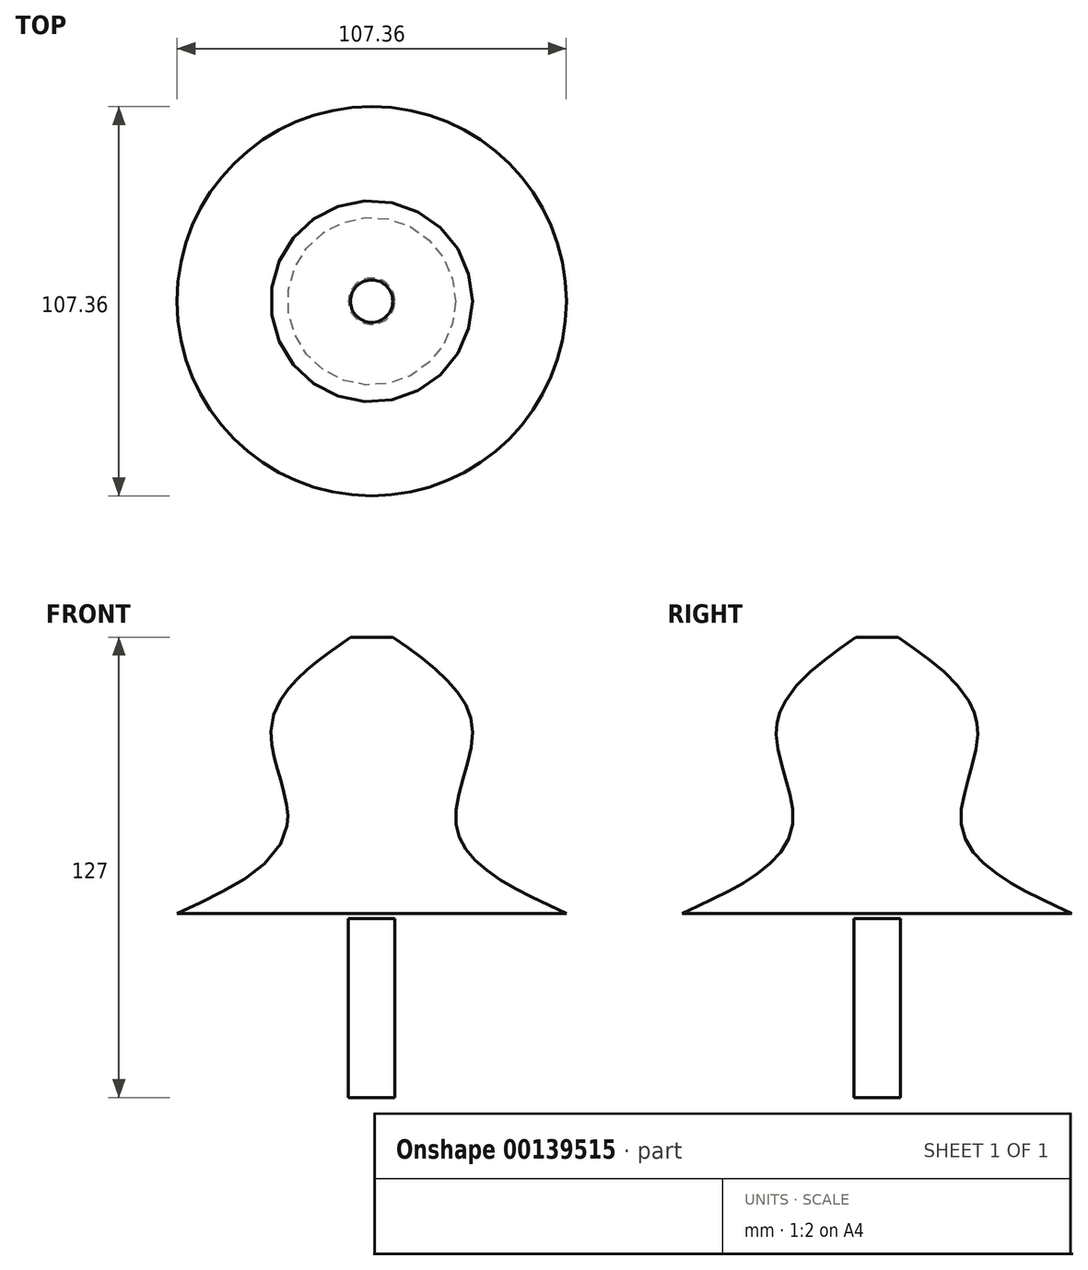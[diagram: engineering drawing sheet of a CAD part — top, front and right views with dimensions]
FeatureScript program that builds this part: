
annotation { "Feature Type Name" : "Feature", "Feature Type Description" : "" }
export const myFeature = defineFeature(function(context is Context, id is Id, definition is map)
    precondition{}
    {
        {
            var Q0;
            Q0=qCreatedBy(makeId("Top.planeOp"),FACE);
            cPlane(context, id + "F0", {"entities" : qUnion([Q0]), "cplaneType" : CPlaneType.OFFSET, "offset" : 25.4 * mm, "width" : 152.4 * mm, "height" : 152.4 * mm});
        }
        {
            var Q0;
            Q0=qCreatedBy(id+"F0.planeOp",FACE);
            cPlane(context, id + "F1", {"entities" : qUnion([Q0]), "cplaneType" : CPlaneType.OFFSET, "offset" : 25.4 * mm, "width" : 152.4 * mm, "height" : 152.4 * mm});
        }
        {
            var Q0;
            Q0=qCreatedBy(makeId("Top.planeOp"),FACE);
            cPlane(context, id + "F2", {"entities" : qUnion([Q0]), "cplaneType" : CPlaneType.OFFSET, "offset" : 25.4 * mm, "oppositeDirection" : true, "width" : 152.4 * mm, "height" : 152.4 * mm});
        }
        {
            var Q0;
            Q0=qCreatedBy(makeId("Top.planeOp"),FACE);
            var sketch = newSketch(context, id + "F3", { "sketchPlane" : qUnion([Q0])});
            skCircle(sketch, "E0", {"center": v(0, 0) * mm, "radius": 23.17 * mm});
            skSolve(sketch);
        }
        {
            var Q0;
            Q0=qCreatedBy(id+"F0.planeOp",FACE);
            var sketch = newSketch(context, id + "F4", { "sketchPlane" : qUnion([Q0])});
            skCircle(sketch, "E1", {"center": v(0, 0) * mm, "radius": 27.75 * mm});
            skSolve(sketch);
        }
        {
            var Q0;
            Q0=qCreatedBy(id+"F1.planeOp",FACE);
            var sketch = newSketch(context, id + "F5", { "sketchPlane" : qUnion([Q0])});
            skCircle(sketch, "E2", {"center": v(0, 0) * mm, "radius": 5.83 * mm});
            skSolve(sketch);
        }
        {
            var Q0;
            Q0=qCreatedBy(id+"F2.planeOp",FACE);
            var sketch = newSketch(context, id + "F6", { "sketchPlane" : qUnion([Q0])});
            skCircle(sketch, "E3", {"center": v(0, 0) * mm, "radius": 53.68 * mm});
            skSolve(sketch);
        }
        {
            var Q0;
            Q0 = qSketchRegion(id + "F5", true);
            var Q1;
            Q1 = qSketchRegion(id + "F4", true);
            var Q2;
            Q2 = qSketchRegion(id + "F3", true);
            var Q3;
            Q3 = qSketchRegion(id + "F6", true);
            loft(context, id + "F7", {"sheetProfilesArray" : [{ "sheetProfileEntities" : qUnion([Q0]) }, { "sheetProfileEntities" : qUnion([Q1]) }, { "sheetProfileEntities" : qUnion([Q2]) }, { "sheetProfileEntities" : qUnion([Q3]) }]});
        }
        {
            var Q0;
            Q0=qCreatedBy(id+"F2.planeOp",FACE);
            cPlane(context, id + "F8", {"entities" : qUnion([Q0]), "cplaneType" : CPlaneType.OFFSET, "offset" : 50.8 * mm, "oppositeDirection" : true, "width" : 152.4 * mm, "height" : 152.4 * mm});
        }
        {
            var Q0;
            Q0=qCreatedBy(id+"F8.planeOp",FACE);
            var sketch = newSketch(context, id + "F9", { "sketchPlane" : qUnion([Q0])});
            skCircle(sketch, "E4", {"center": v(0, 0) * mm, "radius": 6.4 * mm});
            skSolve(sketch);
        }
        {
            var Q0;
            Q0 = qSketchRegion(id + "F9", true);
            extrude(context, id + "F10", {"entities" : qUnion([Q0]), "operationType" : NewBodyOperationType.ADD, "depth" : 49.4 * mm});
        }
    });
